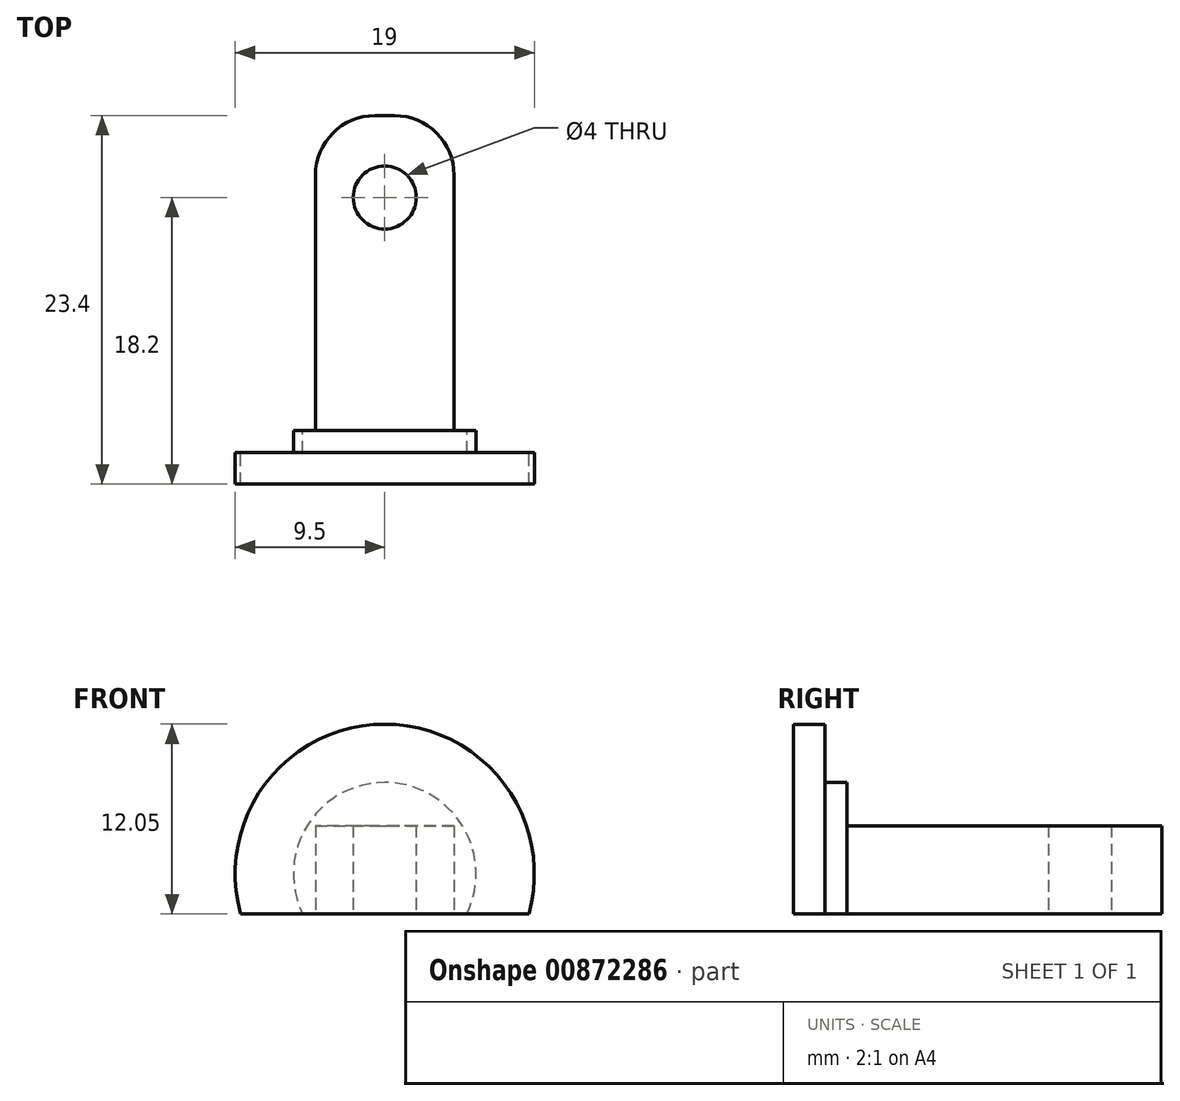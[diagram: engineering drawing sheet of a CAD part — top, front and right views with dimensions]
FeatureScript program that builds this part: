
annotation { "Feature Type Name" : "Feature", "Feature Type Description" : "" }
export const myFeature = defineFeature(function(context is Context, id is Id, definition is map)
    precondition{}
    {
        {
            var Q0;
            Q0=qCreatedBy(makeId("Top.planeOp"),FACE);
            var sketch = newSketch(context, id + "F0", { "sketchPlane" : qUnion([Q0])});
            skLineSegment(sketch, "E0.bottom", {"start": v(-4.4, 10) * mm, "end": v(4.4, 10) * mm});
            skLineSegment(sketch, "E0.top", {"start": v(-4.4, -10) * mm, "end": v(4.4, -10) * mm});
            skLineSegment(sketch, "E0.left", {"start": v(-4.4, 10) * mm, "end": v(-4.4, -10) * mm});
            skLineSegment(sketch, "E0.right", {"start": v(4.4, 10) * mm, "end": v(4.4, -10) * mm});
            skPoint(sketch, "E0.middle", {"position": v(0, 0) * mm});
            skCircle(sketch, "E1", {"center": v(0, 4.8) * mm, "radius": 2 * mm});
            skSolve(sketch);
        }
        {
            var Q0;
            Q0=makeQuery(id+"F0.imprint","IMPRINT",FACE,{"disambiguationData":[TD([[makeQuery(id+"F0.imprint","IMPRINT",EDGE,{"derivedFrom":sQuery(id+"F0.wireOp",EDGE,"E0.bottom")}),-1.0]])]});
            extrude(context, id + "F1", {"entities" : qUnion([Q0]), "depth" : 2.8 * mm, "offsetDistance" : 25 * mm, "hasSecondDirection" : true, "secondDirectionOppositeDirection" : true, "secondDirectionDepth" : 2.8 * mm});
        }
        {
            var Q0;
            Q0=makeQuery(id+"F1.opExtrude","SWEPT_FACE",FACE,{"disambiguationData":[OSD([sQuery(id+"F0.wireOp",EDGE,"E0.top")])]});
            var sketch = newSketch(context, id + "F2", { "sketchPlane" : qUnion([Q0])});
            skArc(sketch, "E2", {"start": v(5.21, -2.8) * mm, "mid": v(0, 5.55) * mm, "end": v(-5.21, -2.8) * mm});
            skArc(sketch, "E3", {"start": v(9.15, -2.8) * mm, "mid": v(0, 9.25) * mm, "end": v(-9.15, -2.8) * mm});
            skLineSegment(sketch, "E4", {"start": v(12.05, -2.8) * mm, "end": v(-12.62, -2.8) * mm, "construction": true});
            skLineSegment(sketch, "E5", {"start": v(9.15, -2.8) * mm, "end": v(-9.15, -2.8) * mm});
            skSolve(sketch);
        }
        {
            var Q0;
            Q0=makeQuery(id+"F2.imprint","IMPRINT",FACE,{"disambiguationData":[TD([[makeQuery(id+"F2.imprint","IMPRINT",EDGE,{"derivedFrom":sQuery(id+"F2.wireOp",EDGE,"E2")}),1.0]])]});
            var Q1;
            {var subQ0=sQuery(id+"F0.wireOp",EDGE,"E0.top");Q1=makeQuery(id+"F2.imprint","IMPRINT",FACE,{"disambiguationData":[TD([[makeQuery(id+"F2.imprint","IMPRINT",EDGE,{"derivedFrom":makeQuery(id+"F1.opExtrude","CAP_EDGE",EDGE,{"disambiguationData":[OSD([subQ0])],"isStart":true})}),1.0]])]});}
            var Q2;
            {var subQ1=sQuery(id+"F0.wireOp",EDGE,"E0.top");Q2=makeQuery(id+"F2.imprint","IMPRINT",FACE,{"disambiguationData":[TD([[makeQuery(id+"F2.imprint","IMPRINT",EDGE,{"derivedFrom":makeQuery(id+"F1.opExtrude","CAP_EDGE",EDGE,{"disambiguationData":[OSD([subQ1])],"isStart":false})}),-1.0]])]});}
            extrude(context, id + "F3", {"entities" : qUnion([Q0, Q1, Q2]), "operationType" : NewBodyOperationType.ADD, "depth" : 1.4 * mm, "offsetDistance" : 25 * mm});
        }
        {
            var Q0;
            {var subQ1=sQuery(id+"F0.wireOp",EDGE,"E0.top");Q0=makeQuery(id+"F2.imprint","IMPRINT",FACE,{"disambiguationData":[TD([[makeQuery(id+"F2.imprint","IMPRINT",EDGE,{"derivedFrom":makeQuery(id+"F1.opExtrude","CAP_EDGE",EDGE,{"disambiguationData":[OSD([subQ1])],"isStart":false})}),-1.0]])]});}
            var Q1;
            {var subQ4=sQuery(id+"F2.wireOp",EDGE,"E2");Q1=makeQuery(id+"F2.imprint","IMPRINT",FACE,{"disambiguationData":[TD([[makeQuery(id+"F2.imprint","IMPRINT",EDGE,{"derivedFrom":subQ4}),1.0]])]});}
            var Q2;
            {var subQ0=sQuery(id+"F2.wireOp",EDGE,"E2");Q2=makeQuery(id+"F2.imprint","IMPRINT",FACE,{"disambiguationData":[TD([[makeQuery(id+"F2.imprint","IMPRINT",EDGE,{"derivedFrom":subQ0}),-1.0]])]});}
            extrude(context, id + "F4", {"entities" : qUnion([Q0, Q1, Q2]), "operationType" : NewBodyOperationType.ADD, "depth" : 3.4 * mm, "offsetDistance" : 25 * mm, "hasSecondDirection" : true, "secondDirectionOppositeDirection" : false, "secondDirectionDepth" : 1.4 * mm});
        }
        {
            var Q0;
            Q0=makeQuery(id+"F1.opExtrude","SWEPT_EDGE",EDGE,{"disambiguationData":[OSD([sQuery(id+"F0.wireOp",EDGE,"E0.bottom"),sQuery(id+"F0.wireOp",EDGE,"E0.right")])]});
            var Q1;
            Q1=makeQuery(id+"F1.opExtrude","SWEPT_EDGE",EDGE,{"disambiguationData":[OSD([sQuery(id+"F0.wireOp",EDGE,"E0.bottom"),sQuery(id+"F0.wireOp",EDGE,"E0.left")])]});
            fillet(context, id + "F5", {"entities" : qUnion([Q0, Q1]), "radius" : 3.8 * mm, "tangentPropagation" : true, "allowEdgeOverflow" : false});
        }
    });
